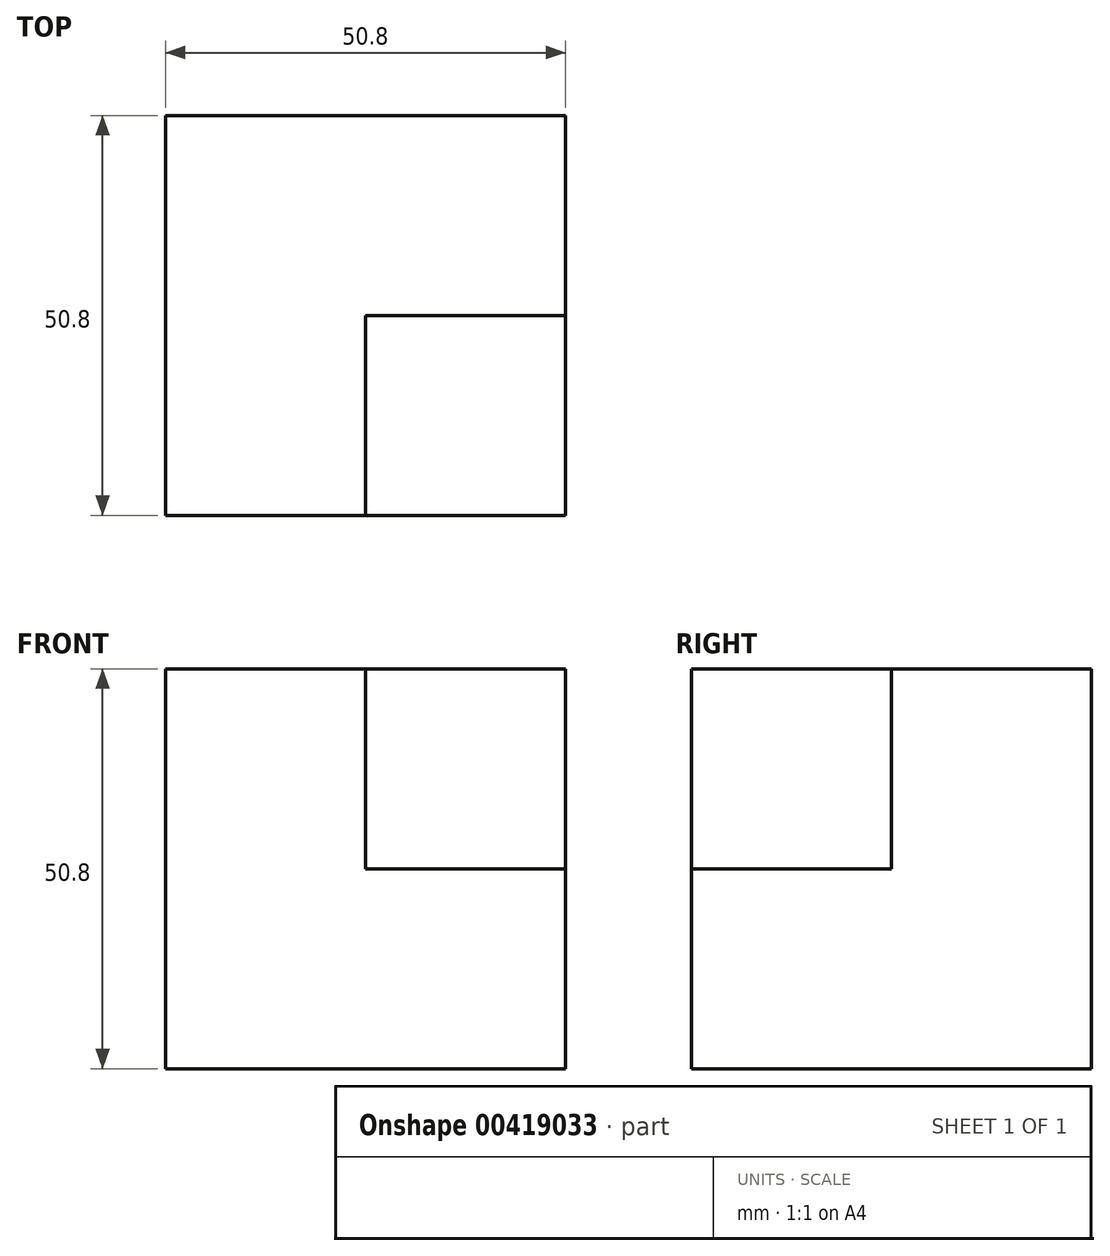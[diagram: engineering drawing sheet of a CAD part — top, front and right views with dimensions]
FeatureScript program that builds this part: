
annotation { "Feature Type Name" : "Feature", "Feature Type Description" : "" }
export const myFeature = defineFeature(function(context is Context, id is Id, definition is map)
    precondition{}
    {
        {
            var Q0;
            Q0=qCreatedBy(makeId("Top.planeOp"),FACE);
            var sketch = newSketch(context, id + "F0", { "sketchPlane" : qUnion([Q0])});
            skLineSegment(sketch, "E0", {"start": v(0, 0) * mm, "end": v(0, -50.8) * mm});
            skLineSegment(sketch, "E1", {"start": v(0, -50.8) * mm, "end": v(-50.8, -50.8) * mm});
            skLineSegment(sketch, "E2", {"start": v(-50.8, -50.8) * mm, "end": v(-50.8, 0) * mm});
            skLineSegment(sketch, "E3", {"start": v(-50.8, 0) * mm, "end": v(0, 0) * mm});
            skSolve(sketch);
        }
        {
            var Q0;
            Q0=makeQuery(id+"F0.imprint","IMPRINT",FACE,{"disambiguationData":[TD([[makeQuery(id+"F0.imprint","IMPRINT",EDGE,{"derivedFrom":sQuery(id+"F0.wireOp",EDGE,"E0")}),-1.0]])]});
            extrude(context, id + "F1", {"entities" : qUnion([Q0]), "depth" : 50.8 * mm});
        }
        {
            var Q0;
            Q0=makeQuery(id+"F1.opExtrude","SWEPT_FACE",FACE,{"disambiguationData":[OSD([sQuery(id+"F0.wireOp",EDGE,"E1")])]});
            var sketch = newSketch(context, id + "F2", { "sketchPlane" : qUnion([Q0])});
            skLineSegment(sketch, "E4", {"start": v(-25.4, 50.8) * mm, "end": v(-25.4, 25.4) * mm});
            skPoint(sketch, "E4.endSnap0", {"position": v(-25.4, 50.8) * mm});
            skLineSegment(sketch, "E5", {"start": v(0, 25.4) * mm, "end": v(-25.4, 25.4) * mm});
            skSolve(sketch);
        }
        {
            var Q0;
            Q0 = qSketchRegion(id + "F2", true);
            var Q1;
            {var subQ0=sQuery(id+"F2.wireOp",EDGE,"E4");Q1=makeQuery(id+"F2.imprint","IMPRINT",FACE,{"disambiguationData":[TD([[makeQuery(id+"F2.imprint","IMPRINT",EDGE,{"derivedFrom":subQ0}),1.0]])]});}
            extrude(context, id + "F3", {"entities" : qUnion([Q0, Q1]), "operationType" : NewBodyOperationType.REMOVE, "oppositeDirection" : true, "depth" : 25.4 * mm});
        }
    });
